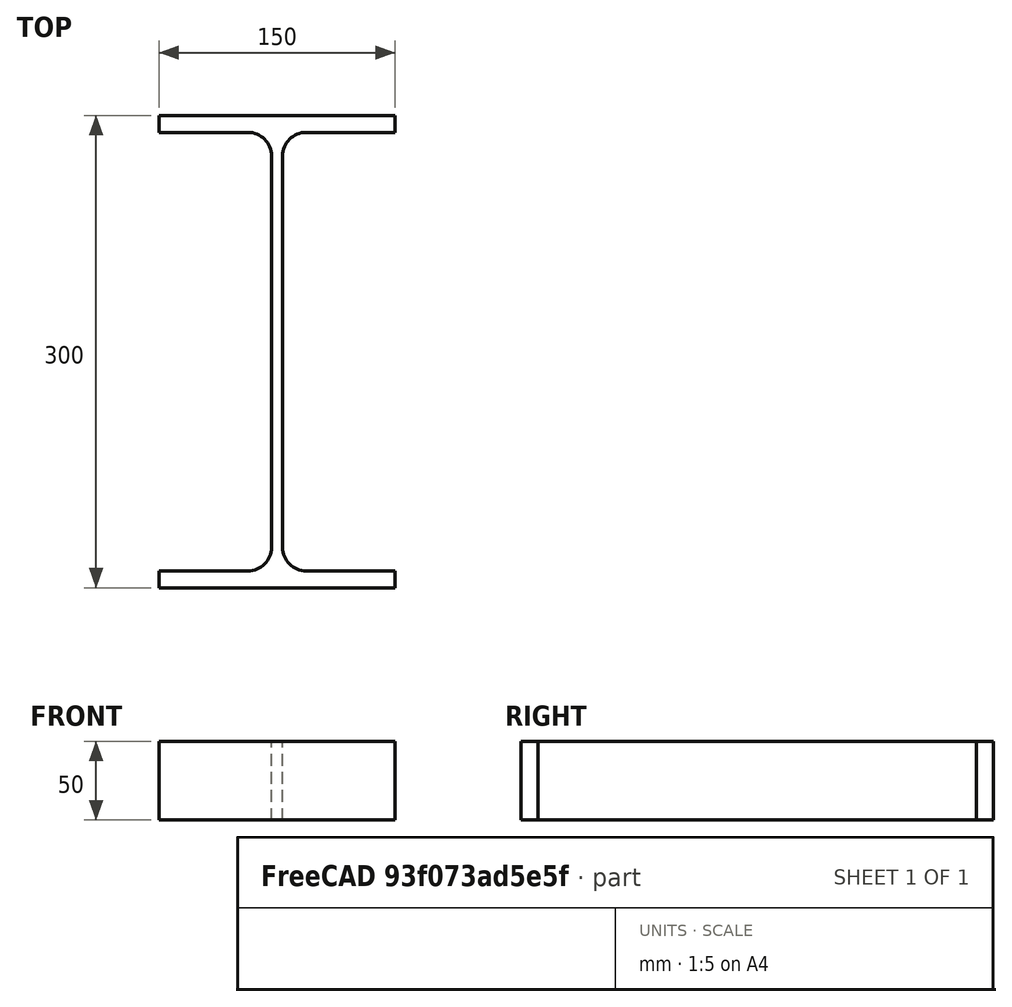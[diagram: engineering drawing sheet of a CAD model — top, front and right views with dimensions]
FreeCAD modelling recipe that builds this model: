
FCSTD DOCUMENT  (FreeCAD 0.15R4671 (Git))
Label: IPE-Profile 300 DIN1025-5 S235JR
License: All rights reserved
LicenseURL: http://en.wikipedia.org/wiki/All_rights_reserved
objects: Sketcher::SketchObject×1, Part::Extrusion×1
note: 2 computed .brp shape members not serialized (recipe doc carries the construction recipe); baked Part::Feature solids carry a one-line shape summary decoded from their .brp

FEATURE [Sketcher::SketchObject] Sketch
  sketch-geometry (16):
    g0: LineSegment StartX=3.55 StartY=-124.3 StartZ=0 EndX=3.55 EndY=124.3 EndZ=0
    g1: LineSegment StartX=18.55 StartY=139.3 StartZ=0 EndX=75 EndY=139.3 EndZ=0
    g2: LineSegment StartX=75 StartY=139.3 StartZ=0 EndX=75 EndY=150 EndZ=0
    g3: LineSegment StartX=75 StartY=150 StartZ=0 EndX=-75 EndY=150 EndZ=0
    g4: LineSegment StartX=-75 StartY=150 StartZ=0 EndX=-75 EndY=139.3 EndZ=0
    g5: LineSegment StartX=-75 StartY=139.3 StartZ=0 EndX=-18.55 EndY=139.3 EndZ=0
    g6: LineSegment StartX=-3.55 StartY=124.3 StartZ=0 EndX=-3.55 EndY=-124.3 EndZ=0
    g7: LineSegment StartX=-18.55 StartY=-139.3 StartZ=0 EndX=-75 EndY=-139.3 EndZ=0
    g8: LineSegment StartX=-75 StartY=-139.3 StartZ=0 EndX=-75 EndY=-150 EndZ=0
    g9: LineSegment StartX=-75 StartY=-150 StartZ=0 EndX=75 EndY=-150 EndZ=0
    g10: LineSegment StartX=75 StartY=-150 StartZ=0 EndX=75 EndY=-139.3 EndZ=0
    g11: LineSegment StartX=75 StartY=-139.3 StartZ=0 EndX=18.55 EndY=-139.3 EndZ=0
    g12: ArcOfCircle CenterX=18.55 CenterY=124.3 CenterZ=0 NormalX=0 NormalY=0 NormalZ=1 Radius=15 StartAngle=1.5708 EndAngle=3.14159
    g13: ArcOfCircle CenterX=18.55 CenterY=-124.3 CenterZ=0 NormalX=0 NormalY=0 NormalZ=1 Radius=15 StartAngle=3.14159 EndAngle=4.71239
    g14: ArcOfCircle CenterX=-18.55 CenterY=124.3 CenterZ=0 NormalX=0 NormalY=0 NormalZ=1 Radius=15 StartAngle=0 EndAngle=1.5708
    g15: ArcOfCircle CenterX=-18.55 CenterY=-124.3 CenterZ=0 NormalX=0 NormalY=0 NormalZ=1 Radius=15 StartAngle=4.71239 EndAngle=6.28319
  constraints (42):
    c: Vertical(g0)
    c: Coincident(g2,g1)
    c: Vertical(g2)
    c: Coincident(g3,g2)
    c: Coincident(g4,g3)
    c: Vertical(g4)
    c: Coincident(g5,g4)
    c: Horizontal(g5)
    c: Vertical(g6)
    c: Horizontal(g7)
    c: Coincident(g8,g7)
    c: Vertical(g8)
    c: Coincident(g9,g8)
    c: Horizontal(g9)
    c: Coincident(g10,g9)
    c: Vertical(g10)
    c: Coincident(g11,g10)
    c: Horizontal(g11)
    c: Tangent(g1,g12) = 1.5708
    c: Tangent(g0,g12) = 1.5708
    c: Tangent(g0,g13) = 1.5708
    c: Tangent(g11,g13) = 1.5708
    c: Tangent(g5,g14) = 1.5708
    c: Tangent(g6,g14) = 1.5708
    c: Tangent(g6,g15) = 1.5708
    c: Tangent(g7,g15) = 1.5708
    c: Equal(g3,g9)
    c: Equal(g2,g4)
    c: Equal(g4,g8)
    c: Equal(g8,g10)
    c: Equal(g12,g14)
    c: Equal(g14,g15)
    c: Equal(g15,g13)
    c: Symmetric(g2,g3,g-2)
    c: Symmetric(g9,g8,g-2)
    c: Symmetric(g0,g6,g-2)
    c: Symmetric(g2,g9,g-1)
    c: DistanceY(g2,g9) = -300
    c: DistanceX(g3) = -150
    c: DistanceX(g0,g6) = -7.1
    c: DistanceY(g2) = 10.7
    c: Radius(g12) = 15
FEATURE [Part::Extrusion] Extrude  label="IPE-Profile 300 DIN1025-5 S235JR"
  Base = -> Sketch
  Dir = (0,0,50)
  Solid = true
